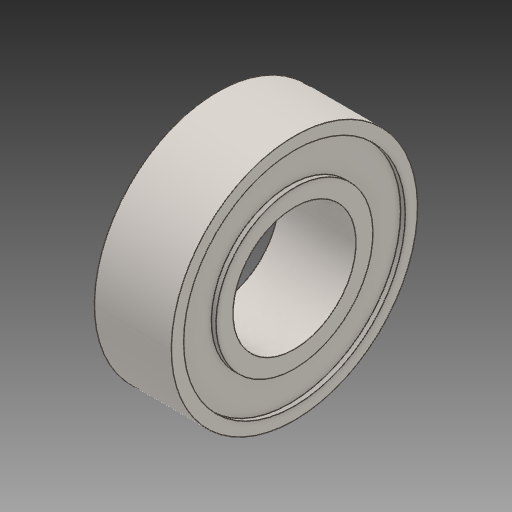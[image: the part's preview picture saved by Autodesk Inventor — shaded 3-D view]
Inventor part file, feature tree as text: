
AUTODESK INVENTOR PART (.ipt)
format: ipt  version: 2017 (Build 210142000, 142)  size: 152,576 bytes
history: mixed  units: mm
features: revolve x1, imported_body x1
ambient origin geometry x8: Origin, YZ Plane, XZ Plane, XY Plane, X Axis, Y Axis, Z Axis, Center Point
bodies: Solid1 (imported_parasolid)
feature tree (2):
  revolve  "Revolve1"  [1 undecoded]
  imported_body  NMx_Import_Brep_tag  [imported B-rep: ~12 faces, bbox_mm=[5.0, 0.0, 4.0]]
note: 1 required parameter value undecoded (feature->parameter linkage not recoverable at this tier; creation-order binding heuristic only, values carry confidence <= 0.55)
